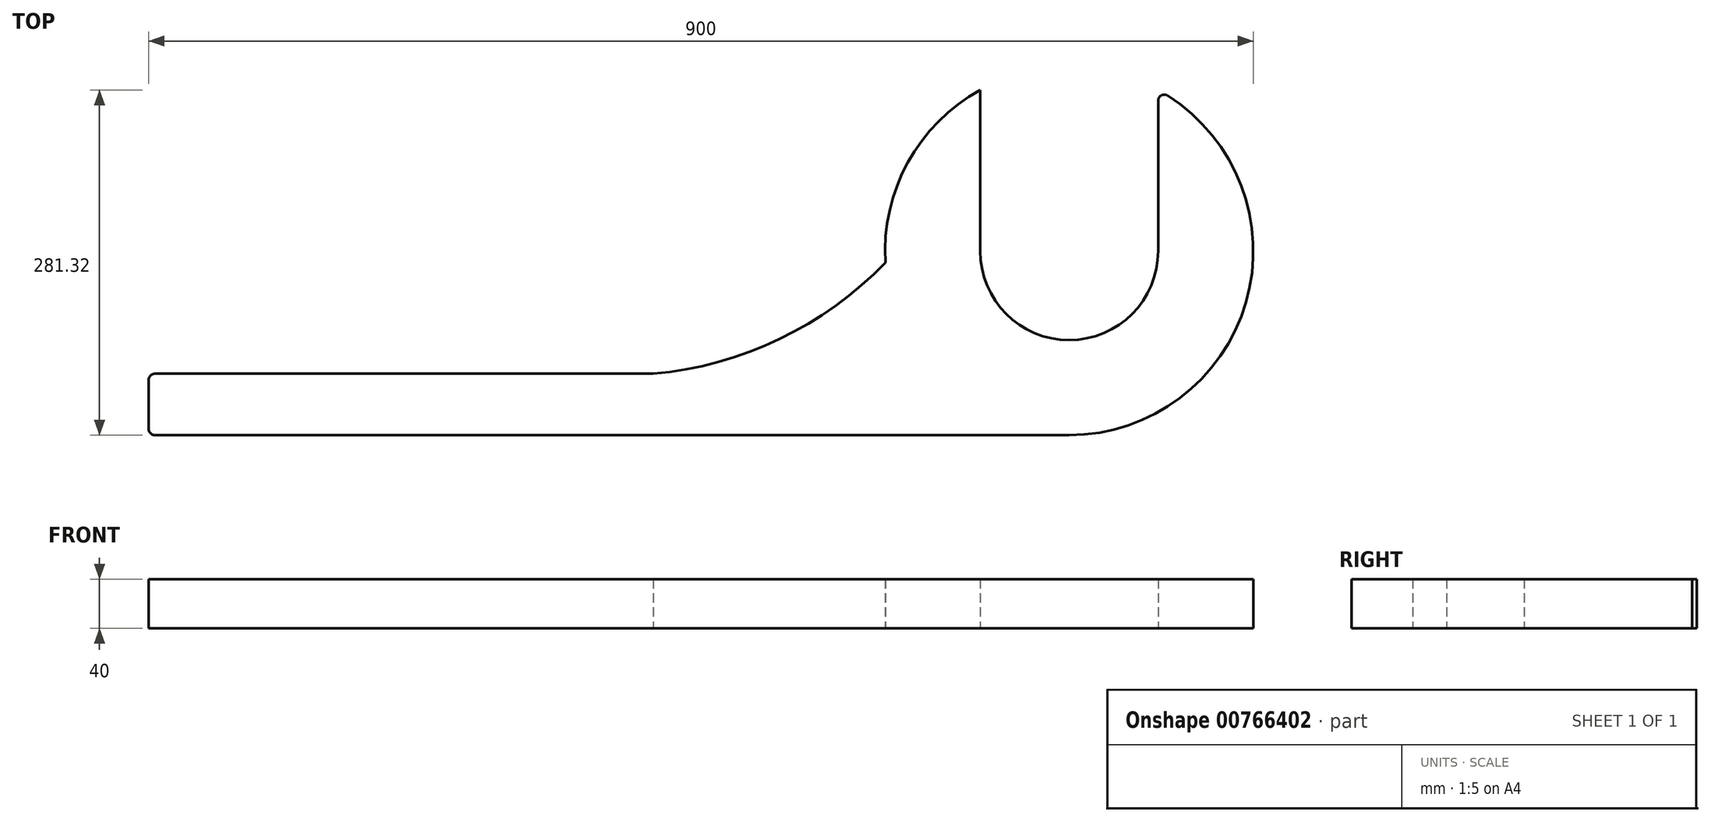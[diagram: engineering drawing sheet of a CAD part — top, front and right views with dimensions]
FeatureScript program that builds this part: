
annotation { "Feature Type Name" : "Feature", "Feature Type Description" : "" }
export const myFeature = defineFeature(function(context is Context, id is Id, definition is map)
    precondition{}
    {
        {
            var Q0;
            Q0=qCreatedBy(makeId("Top.planeOp"),FACE);
            var sketch = newSketch(context, id + "F0", { "sketchPlane" : qUnion([Q0])});
            skCircle(sketch, "E0", {"center": v(0, 0) * mm, "radius": 72.5 * mm});
            skCircle(sketch, "E1", {"center": v(0, 0) * mm, "radius": 150 * mm});
            skLineSegment(sketch, "E2", {"start": v(-72.5, 0) * mm, "end": v(-72.5, 131.32) * mm});
            skLineSegment(sketch, "E3", {"start": v(72.5, 0) * mm, "end": v(72.5, 131.32) * mm});
            skLineSegment(sketch, "E4.bottom", {"start": v(0, -150) * mm, "end": v(-750, -150) * mm});
            skLineSegment(sketch, "E4.top", {"start": v(0, -100) * mm, "end": v(-750, -100) * mm});
            skLineSegment(sketch, "E4.left", {"start": v(0, -150) * mm, "end": v(0, -100) * mm});
            skLineSegment(sketch, "E4.right", {"start": v(-750, -150) * mm, "end": v(-750, -100) * mm});
            skArc(sketch, "E5", {"start": v(-338.85, -100) * mm, "mid": v(-236.1, -71.74) * mm, "end": v(-149.7, -9.35) * mm});
            skSolve(sketch);
        }
        {
            var Q0;
            Q0 = qSketchRegion(id + "F0", true);
            extrude(context, id + "F1", {"entities" : qUnion([Q0]), "depth" : 40 * mm, "offsetDistance" : 25 * mm});
        }
        {
            var Q0;
            {var subQ0=sQuery(id+"F0.wireOp",EDGE,"E2");Q0=makeQuery(id+"F0.imprint","IMPRINT",FACE,{"disambiguationData":[TD([[makeQuery(id+"F0.imprint","IMPRINT",EDGE,{"derivedFrom":subQ0}),-1.0]])]});}
            extrude(context, id + "F2", {"entities" : qUnion([Q0]), "operationType" : NewBodyOperationType.REMOVE, "depth" : 40 * mm, "offsetDistance" : 25 * mm});
        }
        {
            var Q0;
            Q0=makeQuery(id+"F1.opExtrude","SWEPT_EDGE",EDGE,{"disambiguationData":[OSD([sQuery(id+"F0.wireOp",EDGE,"E4.bottom"),sQuery(id+"F0.wireOp",EDGE,"E4.right")])]});
            var Q1;
            Q1=makeQuery(id+"F2.boolean.opBoolean","COPY",EDGE,{"derivedFrom":makeQuery(id+"F2.opExtrude","SWEPT_EDGE",EDGE,{"disambiguationData":[OSD([sQuery(id+"F0.wireOp",EDGE,"E1"),sQuery(id+"F0.wireOp",EDGE,"E2")])]})});
            var Q2;
            Q2=makeQuery(id+"F2.boolean.opBoolean","COPY",EDGE,{"derivedFrom":makeQuery(id+"F2.opExtrude","SWEPT_EDGE",EDGE,{"disambiguationData":[OSD([sQuery(id+"F0.wireOp",EDGE,"E1"),sQuery(id+"F0.wireOp",EDGE,"E3")])]})});
            var Q3;
            Q3=makeQuery(id+"F1.opExtrude","SWEPT_EDGE",EDGE,{"disambiguationData":[OSD([sQuery(id+"F0.wireOp",EDGE,"E4.top"),sQuery(id+"F0.wireOp",EDGE,"E4.right")])]});
            fillet(context, id + "F3", {"entities" : qUnion([Q0, Q1, Q2, Q3]), "radius" : 5 * mm, "tangentPropagation" : true, "allowEdgeOverflow" : false});
        }
    });
